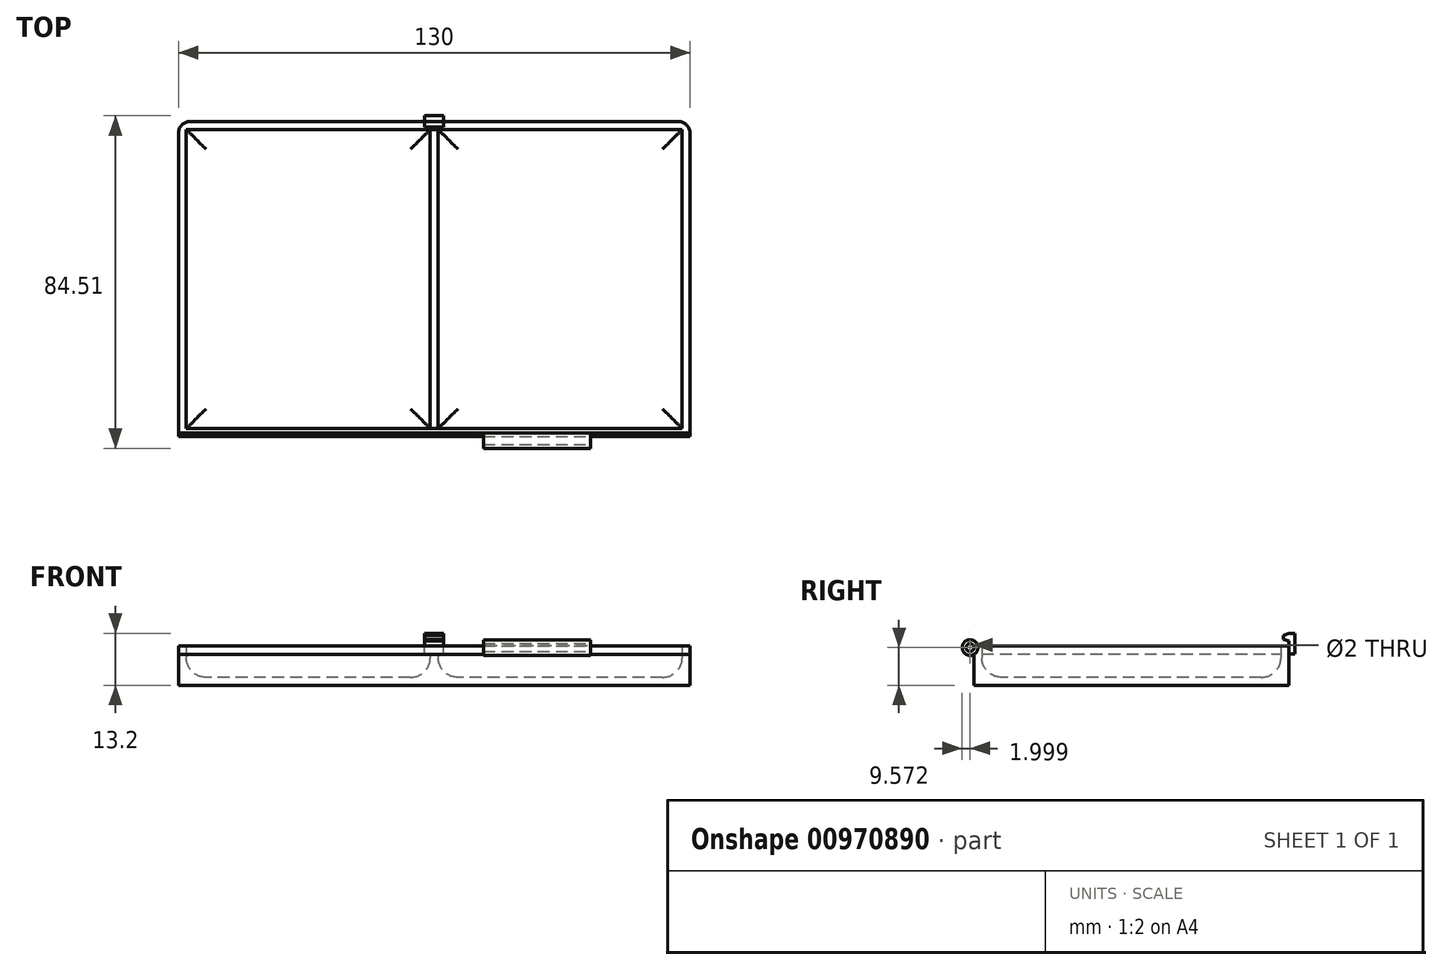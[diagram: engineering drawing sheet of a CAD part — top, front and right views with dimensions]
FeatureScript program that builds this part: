
annotation { "Feature Type Name" : "Feature", "Feature Type Description" : "" }
export const myFeature = defineFeature(function(context is Context, id is Id, definition is map)
    precondition{}
    {
        {
            var Q0;
            Q0=qCreatedBy(makeId("Top.planeOp"),FACE);
            var sketch = newSketch(context, id + "F0", { "sketchPlane" : qUnion([Q0])});
            skLineSegment(sketch, "E0.bottom", {"start": v(0, 0) * mm, "end": v(-130, 0) * mm});
            skLineSegment(sketch, "E0.top", {"start": v(0, 80) * mm, "end": v(-130, 80) * mm});
            skLineSegment(sketch, "E0.left", {"start": v(0, 0) * mm, "end": v(0, 80) * mm});
            skLineSegment(sketch, "E0.right", {"start": v(-130, 0) * mm, "end": v(-130, 80) * mm});
            skLineSegment(sketch, "E1", {"start": v(-65, 0) * mm, "end": v(-65, 80) * mm});
            skArc(sketch, "E2.0.startCap", {"start": v(-64, 0) * mm, "mid": v(-65, -1) * mm, "end": v(-66, 0) * mm});
            skArc(sketch, "E2.0.endCap", {"start": v(-66, 80) * mm, "mid": v(-65, 81) * mm, "end": v(-64, 80) * mm});
            skLineSegment(sketch, "E2.0.left", {"start": v(-66, 0) * mm, "end": v(-66, 80) * mm});
            skLineSegment(sketch, "E2.0.right", {"start": v(-64, 0) * mm, "end": v(-64, 80) * mm});
            skSolve(sketch);
        }
        {
            var Q0;
            Q0=makeQuery(id+"F0.imprint","IMPRINT",FACE,{"disambiguationData":[TD([[makeQuery(id+"F0.imprint","IMPRINT",EDGE,{"derivedFrom":sQuery(id+"F0.wireOp",EDGE,"E0.bottom")}),-1.0]])]});
            extrude(context, id + "F1", {"entities" : qUnion([Q0]), "depth" : 10 * mm, "offsetDistance" : 25 * mm});
        }
        {
            var Q0;
            Q0=makeQuery(id+"F1.opExtrude","CAP_FACE",FACE,{"disambiguationData":[OSD([sQuery(id+"F0.wireOp",EDGE,"E0.bottom"),sQuery(id+"F0.wireOp",EDGE,"E0.top"),sQuery(id+"F0.wireOp",EDGE,"E0.left"),sQuery(id+"F0.wireOp",EDGE,"E0.right")])],"isStart":false});
            shell(context, id + "F2", {"entities" : qUnion([Q0]), "thickness" : 2 * mm});
        }
        {
            var Q0;
            {var subQ0=sQuery(id+"F0.wireOp",EDGE,"E1");Q0=makeQuery(id+"F0.imprint","IMPRINT",FACE,{"disambiguationData":[TD([[makeQuery(id+"F0.imprint","IMPRINT",EDGE,{"derivedFrom":subQ0}),1.0]])]});}
            var Q1;
            {var subQ0=sQuery(id+"F0.wireOp",EDGE,"E1");Q1=makeQuery(id+"F0.imprint","IMPRINT",FACE,{"disambiguationData":[TD([[makeQuery(id+"F0.imprint","IMPRINT",EDGE,{"derivedFrom":subQ0}),-1.0]])]});}
            var Q2;
            Q2=makeQuery(id+"F1.opExtrude","CAP_FACE",FACE,{"disambiguationData":[OSD([sQuery(id+"F0.wireOp",EDGE,"E0.bottom"),sQuery(id+"F0.wireOp",EDGE,"E0.top"),sQuery(id+"F0.wireOp",EDGE,"E0.left"),sQuery(id+"F0.wireOp",EDGE,"E0.right")])],"isStart":false});
            extrude(context, id + "F3", {"entities" : qUnion([Q0, Q1]), "operationType" : NewBodyOperationType.ADD, "depth" : 8 * mm, "endBoundEntityFace" : qUnion([Q2]), "offsetDistance" : 25 * mm});
        }
        {
            var Q0;
            Q0=makeQuery(id+"F1.opExtrude","SWEPT_FACE",FACE,{"disambiguationData":[OSD([sQuery(id+"F0.wireOp",EDGE,"E0.left")])]});
            var sketch = newSketch(context, id + "F4", { "sketchPlane" : qUnion([Q0])});
            skCircle(sketch, "E3", {"center": v(-1.01, 9.57) * mm, "radius": 2 * mm});
            skCircle(sketch, "E4.0", {"center": v(-1.01, 9.57) * mm, "radius": 1 * mm});
            skLineSegment(sketch, "E5", {"start": v(-1.01, 9.57) * mm, "end": v(-1.01, 8.57) * mm, "construction": true});
            skLineSegment(sketch, "E6", {"start": v(-1.01, 9.57) * mm, "end": v(-0.3, 8.86) * mm, "construction": true});
            skCircle(sketch, "E7.0", {"center": v(-1.01, 9.57) * mm, "radius": 1.9 * mm});
            skSolve(sketch);
        }
        {
            var Q0;
            {var subQ0=sQuery(id+"F4.wireOp",EDGE,"E3");var subQ1=sQuery(id+"F0.wireOp",EDGE,"E0.left");var subQ4=makeQuery(id+"F1.opExtrude","CAP_EDGE",EDGE,{"disambiguationData":[OSD([subQ1])],"isStart":false});var subQ5=makeQuery(id+"F4.imprint","INTERSECT",VERTEX,{"derivedFrom":[subQ4,subQ0]});Q0=makeQuery(id+"F4.imprint","IMPRINT",FACE,{"disambiguationData":[TD([[makeQuery(id+"F4.imprint","IMPRINT",EDGE,{"disambiguationData":[TD([[subQ5,1.0]])],"derivedFrom":subQ4}),-1.0]])]});}
            var Q1;
            {var subQ0=sQuery(id+"F4.wireOp",EDGE,"E7.0");var subQ1=sQuery(id+"F0.wireOp",EDGE,"E0.left");var subQ4=makeQuery(id+"F1.opExtrude","CAP_EDGE",EDGE,{"disambiguationData":[OSD([subQ1])],"isStart":false});var subQ5=makeQuery(id+"F4.imprint","INTERSECT",VERTEX,{"derivedFrom":[subQ4,subQ0]});Q1=makeQuery(id+"F4.imprint","IMPRINT",FACE,{"disambiguationData":[TD([[makeQuery(id+"F4.imprint","IMPRINT",EDGE,{"disambiguationData":[TD([[subQ5,1.0]])],"derivedFrom":subQ0}),1.0]])]});}
            extrude(context, id + "F5", {"entities" : qUnion([Q0, Q1]), "operationType" : NewBodyOperationType.REMOVE, "endBound" : BoundingType.THROUGH_ALL, "oppositeDirection" : true, "depth" : 25 * mm, "offsetDistance" : 25 * mm});
        }
        {
            var Q0;
            {var subQ0=sQuery(id+"F4.wireOp",EDGE,"E3");var subQ1=sQuery(id+"F0.wireOp",EDGE,"E0.left");var subQ4=makeQuery(id+"F1.opExtrude","CAP_EDGE",EDGE,{"disambiguationData":[OSD([subQ1])],"isStart":false});var subQ5=makeQuery(id+"F4.imprint","INTERSECT",VERTEX,{"derivedFrom":[subQ4,subQ0]});Q0=makeQuery(id+"F4.imprint","IMPRINT",FACE,{"disambiguationData":[TD([[makeQuery(id+"F4.imprint","IMPRINT",EDGE,{"disambiguationData":[TD([[subQ5,1.0]])],"derivedFrom":subQ4}),-1.0]])]});}
            var Q1;
            {var subQ0=sQuery(id+"F4.wireOp",EDGE,"E3");var subQ1=sQuery(id+"F0.wireOp",EDGE,"E0.left");var subQ4=makeQuery(id+"F1.opExtrude","CAP_EDGE",EDGE,{"disambiguationData":[OSD([subQ1])],"isStart":false});var subQ5=makeQuery(id+"F4.imprint","INTERSECT",VERTEX,{"derivedFrom":[subQ4,subQ0]});Q1=makeQuery(id+"F4.imprint","IMPRINT",FACE,{"disambiguationData":[TD([[makeQuery(id+"F4.imprint","IMPRINT",EDGE,{"disambiguationData":[TD([[subQ5,1.0]])],"derivedFrom":subQ4}),1.0]])]});}
            var Q2;
            {var subQ0=sQuery(id+"F4.wireOp",EDGE,"E7.0");var subQ1=sQuery(id+"F0.wireOp",EDGE,"E0.left");var subQ4=makeQuery(id+"F1.opExtrude","CAP_EDGE",EDGE,{"disambiguationData":[OSD([subQ1])],"isStart":false});var subQ5=makeQuery(id+"F4.imprint","INTERSECT",VERTEX,{"derivedFrom":[subQ4,subQ0]});Q2=makeQuery(id+"F4.imprint","IMPRINT",FACE,{"disambiguationData":[TD([[makeQuery(id+"F4.imprint","IMPRINT",EDGE,{"disambiguationData":[TD([[subQ5,1.0]])],"derivedFrom":subQ0}),1.0]])]});}
            var Q3;
            Q3=makeQuery(id+"F4.imprint","IMPRINT",FACE,{"disambiguationData":[TD([[makeQuery(id+"F4.imprint","IMPRINT",EDGE,{"derivedFrom":sQuery(id+"F4.wireOp",EDGE,"E4.0")}),-1.0]])]});
            extrude(context, id + "F6", {"entities" : qUnion([Q0, Q1, Q2, Q3]), "operationType" : NewBodyOperationType.ADD, "oppositeDirection" : true, "depth" : (25.25 + 27.25) * mm, "offsetDistance" : 25 * mm, "hasSecondDirection" : true, "secondDirectionOppositeDirection" : true, "secondDirectionDepth" : 25.25 * mm});
        }
        {
            var Q0;
            Q0=makeQuery(id+"F1.opExtrude","SWEPT_FACE",FACE,{"disambiguationData":[OSD([sQuery(id+"F0.wireOp",EDGE,"E0.right")])]});
            var Q1;
            Q1=makeQuery(id+"F1.opExtrude","SWEPT_FACE",FACE,{"disambiguationData":[OSD([sQuery(id+"F0.wireOp",EDGE,"E0.left")])]});
            cPlane(context, id + "F7", {"entities" : qUnion([Q0, Q1]), "cplaneType" : CPlaneType.MID_PLANE, "offset" : 25 * mm, "width" : 150 * mm, "height" : 150 * mm});
        }
        {
            var Q0;
            Q0=qCreatedBy(id+"F7.planeOp",FACE);
            var sketch = newSketch(context, id + "F8", { "sketchPlane" : qUnion([Q0])});
            skPoint(sketch, "E8.0", {"position": v(-80, 10) * mm});
            skLineSegment(sketch, "E9.bottom", {"start": v(-80, 10) * mm, "end": v(-81.5, 10) * mm});
            skLineSegment(sketch, "E9.top", {"start": v(-80, 13.2) * mm, "end": v(-81.5, 13.2) * mm});
            skLineSegment(sketch, "E9.left", {"start": v(-80, 10) * mm, "end": v(-80, 13.2) * mm});
            skLineSegment(sketch, "E9.right", {"start": v(-81.5, 10) * mm, "end": v(-81.5, 13.2) * mm});
            skLineSegment(sketch, "E10.top", {"start": v(-80, 8) * mm, "end": v(-81.5, 8) * mm});
            skLineSegment(sketch, "E10.left", {"start": v(-80, 10) * mm, "end": v(-80, 8) * mm});
            skLineSegment(sketch, "E10.right", {"start": v(-81.5, 10) * mm, "end": v(-81.5, 8) * mm});
            skLineSegment(sketch, "E11", {"start": v(-80, 13.2) * mm, "end": v(-78.6, 12.7) * mm});
            skLineSegment(sketch, "E12", {"start": v(-78.6, 12.7) * mm, "end": v(-78.6, 11.7) * mm});
            skLineSegment(sketch, "E13", {"start": v(-78.6, 11.7) * mm, "end": v(-80, 11.2) * mm});
            skSolve(sketch);
        }
        {
            var Q0;
            Q0=makeQuery(id+"F8.imprint","IMPRINT",FACE,{"disambiguationData":[TD([[makeQuery(id+"F8.imprint","IMPRINT",EDGE,{"derivedFrom":sQuery(id+"F8.wireOp",EDGE,"E9.left")}),-1.0]])]});
            var Q1;
            Q1=makeQuery(id+"F8.imprint","IMPRINT",FACE,{"disambiguationData":[TD([[makeQuery(id+"F8.imprint","IMPRINT",EDGE,{"derivedFrom":sQuery(id+"F8.wireOp",EDGE,"E9.top")}),1.0]])]});
            var Q2;
            Q2=makeQuery(id+"F8.imprint","IMPRINT",FACE,{"disambiguationData":[TD([[makeQuery(id+"F8.imprint","IMPRINT",EDGE,{"derivedFrom":sQuery(id+"F8.wireOp",EDGE,"E9.bottom")}),1.0]])]});
            extrude(context, id + "F9", {"entities" : qUnion([Q0, Q1, Q2]), "operationType" : NewBodyOperationType.ADD, "endBound" : BoundingType.SYMMETRIC, "depth" : 4.8 * mm, "offsetDistance" : 25 * mm});
        }
        {
            var Q0;
            {var subQ0=sQuery(id+"F0.wireOp",EDGE,"E0.bottom");var subQ1=sQuery(id+"F0.wireOp",EDGE,"E0.top");var subQ2=sQuery(id+"F0.wireOp",EDGE,"E0.left");Q0=makeQuery(id+"F3.boolean.opBoolean","SPLIT",FACE,{"disambiguationData":[TD([makeQuery(id+"F2.opShell","OFFSET_FACE",FACE,{"disambiguationData":[OSD([subQ2])]})])],"derivedFrom":makeQuery(id+"F2.opShell","OFFSET_FACE",FACE,{"disambiguationData":[OSD([subQ0,subQ1,subQ2,sQuery(id+"F0.wireOp",EDGE,"E0.right")])]})});}
            var Q1;
            {var subQ0=sQuery(id+"F0.wireOp",EDGE,"E0.bottom");var subQ1=sQuery(id+"F0.wireOp",EDGE,"E0.top");var subQ2=sQuery(id+"F0.wireOp",EDGE,"E0.right");Q1=makeQuery(id+"F3.boolean.opBoolean","SPLIT",FACE,{"disambiguationData":[TD([makeQuery(id+"F2.opShell","OFFSET_FACE",FACE,{"disambiguationData":[OSD([subQ2])]})])],"derivedFrom":makeQuery(id+"F2.opShell","OFFSET_FACE",FACE,{"disambiguationData":[OSD([subQ0,subQ1,sQuery(id+"F0.wireOp",EDGE,"E0.left"),subQ2])]})});}
            fillet(context, id + "F10", {"entities" : qUnion([Q0, Q1]), "radius" : 5 * mm, "tangentPropagation" : true, "allowEdgeOverflow" : false});
        }
        {
            var Q0;
            Q0=makeQuery(id+"F1.opExtrude","SWEPT_EDGE",EDGE,{"disambiguationData":[OSD([sQuery(id+"F0.wireOp",EDGE,"E0.top"),sQuery(id+"F0.wireOp",EDGE,"E0.right")])]});
            var Q1;
            Q1=makeQuery(id+"F1.opExtrude","SWEPT_EDGE",EDGE,{"disambiguationData":[OSD([sQuery(id+"F0.wireOp",EDGE,"E0.top"),sQuery(id+"F0.wireOp",EDGE,"E0.left")])]});
            fillet(context, id + "F11", {"entities" : qUnion([Q0, Q1]), "radius" : 3 * mm, "tangentPropagation" : true, "allowEdgeOverflow" : false});
        }
    });
